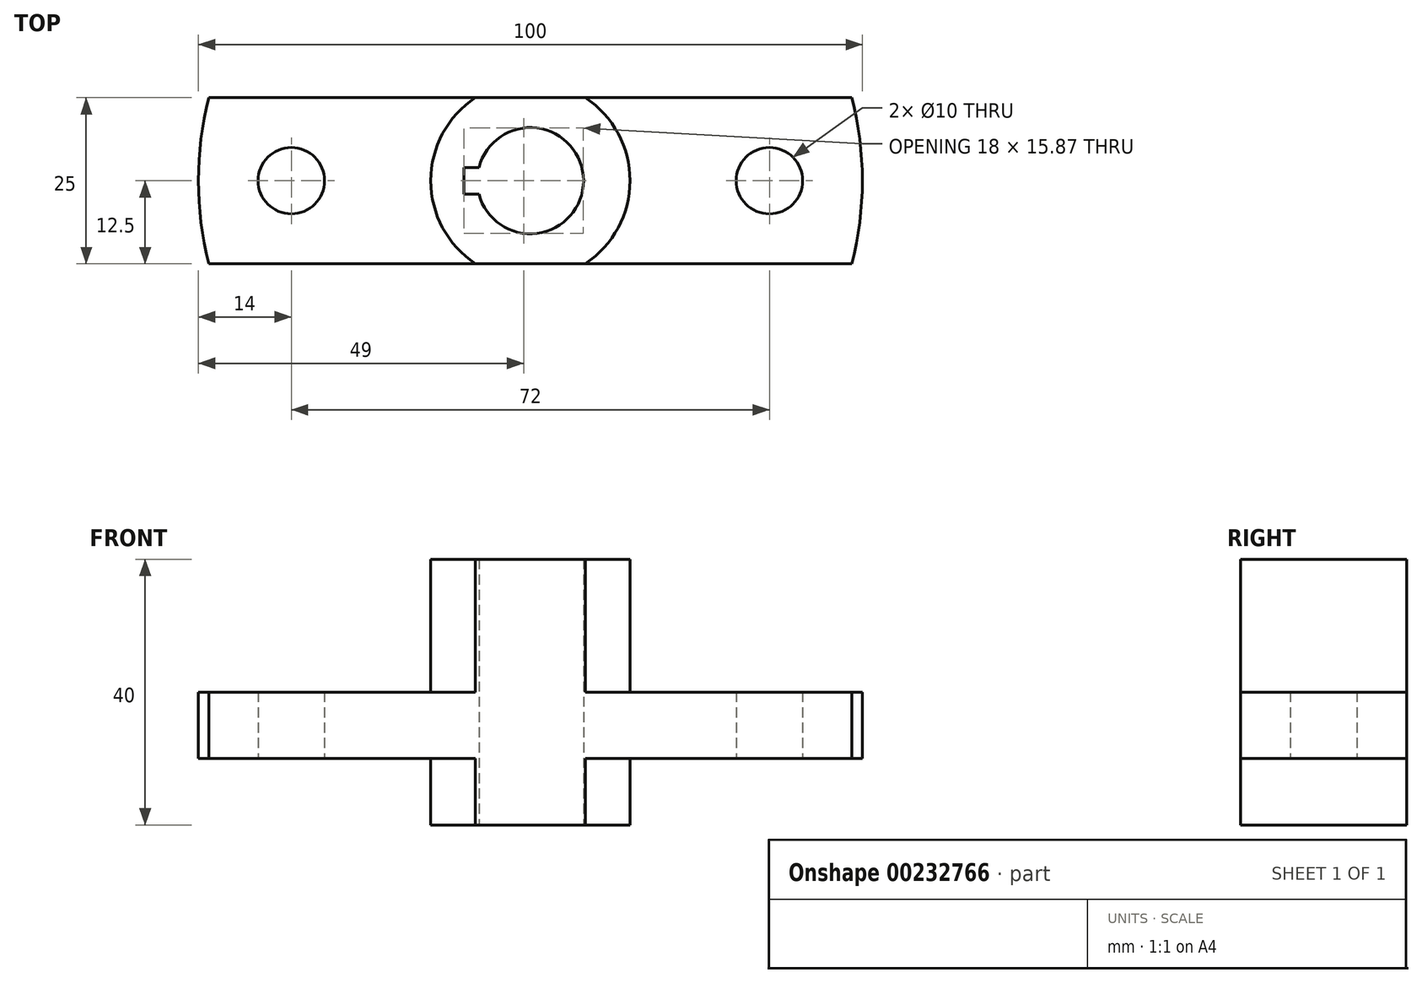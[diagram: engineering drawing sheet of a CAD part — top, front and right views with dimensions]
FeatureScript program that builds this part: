
annotation { "Feature Type Name" : "Feature", "Feature Type Description" : "" }
export const myFeature = defineFeature(function(context is Context, id is Id, definition is map)
    precondition{}
    {
        {
            var Q0;
            Q0=qCreatedBy(makeId("Top.planeOp"),FACE);
            var sketch = newSketch(context, id + "F0", { "sketchPlane" : qUnion([Q0])});
            skArc(sketch, "E0", {"start": v(-7.75, -2) * mm, "mid": v(8, 0) * mm, "end": v(-7.75, 2) * mm});
            skLineSegment(sketch, "E1", {"start": v(-7.75, 2) * mm, "end": v(-10, 2) * mm});
            skLineSegment(sketch, "E2", {"start": v(-10, 2) * mm, "end": v(-10, -2) * mm});
            skLineSegment(sketch, "E3", {"start": v(-10, -2) * mm, "end": v(-7.75, -2) * mm});
            skArc(sketch, "E4", {"start": v(-8.3, 12.5) * mm, "mid": v(-15, 0) * mm, "end": v(-8.3, -12.5) * mm});
            skArc(sketch, "E5", {"start": v(-48.41, 12.5) * mm, "mid": v(-50, 0) * mm, "end": v(-48.41, -12.5) * mm});
            skLineSegment(sketch, "E6.bottom", {"start": v(48.41, -12.5) * mm, "end": v(-48.41, -12.5) * mm});
            skLineSegment(sketch, "E6.top", {"start": v(48.41, 12.5) * mm, "end": v(-48.41, 12.5) * mm});
            skCircle(sketch, "E7", {"center": v(36, 0) * mm, "radius": 5 * mm});
            skCircle(sketch, "E8.MirrorC", {"center": v(-36, 0) * mm, "radius": 5 * mm});
            skArc(sketch, "E9.trimOffspring", {"start": v(48.41, -12.5) * mm, "mid": v(50, 0) * mm, "end": v(48.41, 12.5) * mm});
            skArc(sketch, "E10.trimOffspring", {"start": v(8.3, -12.5) * mm, "mid": v(15, 0) * mm, "end": v(8.3, 12.5) * mm});
            skSolve(sketch);
        }
        {
            var Q0;
            Q0=makeQuery(id+"F0.imprint","IMPRINT",FACE,{"disambiguationData":[TD([[makeQuery(id+"F0.imprint","IMPRINT",EDGE,{"derivedFrom":sQuery(id+"F0.wireOp",EDGE,"E0")}),-1.0]])]});
            extrude(context, id + "F1", {"entities" : qUnion([Q0]), "depth" : 30 * mm, "hasSecondDirection" : true, "secondDirectionOppositeDirection" : true, "secondDirectionDepth" : 10 * mm});
        }
        {
            var Q0;
            {var subQ1=sQuery(id+"F0.wireOp",EDGE,"E4");Q0=makeQuery(id+"F0.imprint","IMPRINT",FACE,{"disambiguationData":[TD([[makeQuery(id+"F0.imprint","IMPRINT",EDGE,{"derivedFrom":subQ1}),-1.0]])]});}
            var Q1;
            Q1=makeQuery(id+"F0.imprint","IMPRINT",FACE,{"disambiguationData":[TD([[makeQuery(id+"F0.imprint","IMPRINT",EDGE,{"derivedFrom":sQuery(id+"F0.wireOp",EDGE,"E7")}),-1.0]])]});
            extrude(context, id + "F2", {"entities" : qUnion([Q0, Q1]), "operationType" : NewBodyOperationType.ADD, "depth" : 10 * mm});
        }
    });
